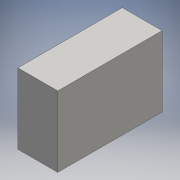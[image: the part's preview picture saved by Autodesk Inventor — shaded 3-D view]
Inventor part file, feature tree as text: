
AUTODESK INVENTOR PART (.ipt)
format: ipt  version: 2016 (Build 200138000, 138)  size: 81,408 bytes
history: native  units: mm
features: other x1, extrude x1, sketch x1
ambient origin geometry x8: Origin, YZ Plane, XZ Plane, XY Plane, X Axis, Y Axis, Z Axis, Center Point
bodies: Body1 (feature_tree)
feature tree (3):
  other  "Sólido1"
  extrude  "Extrusión1"  Depth=23.0mm
  sketch  "Boceto1"  dims[d0=34.0mm d1=23.0mm d2=13.0mm d3=0.0mm]
